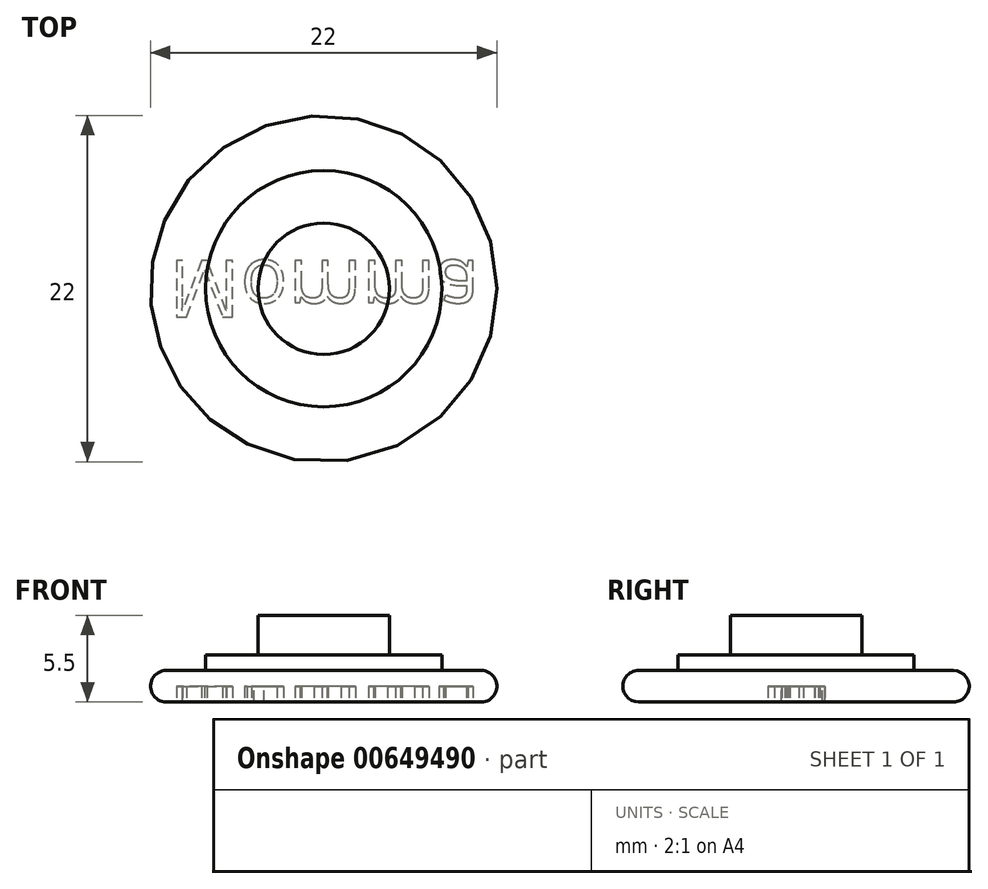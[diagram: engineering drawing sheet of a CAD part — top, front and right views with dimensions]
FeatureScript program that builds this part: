
annotation { "Feature Type Name" : "Feature", "Feature Type Description" : "" }
export const myFeature = defineFeature(function(context is Context, id is Id, definition is map)
    precondition{}
    {
        {
            var Q0;
            Q0=qCreatedBy(makeId("Top.planeOp"),FACE);
            var sketch = newSketch(context, id + "F0", { "sketchPlane" : qUnion([Q0])});
            skCircle(sketch, "E0", {"center": v(0, 0) * mm, "radius": 11 * mm});
            skCircle(sketch, "E1", {"center": v(0, 0) * mm, "radius": 7.5 * mm});
            skCircle(sketch, "E2", {"center": v(0, 0) * mm, "radius": 4.17 * mm});
            skSolve(sketch);
        }
        {
            var Q0;
            Q0=makeQuery(id+"F0.imprint","IMPRINT",FACE,{"disambiguationData":[TD([[makeQuery(id+"F0.imprint","IMPRINT",EDGE,{"derivedFrom":sQuery(id+"F0.wireOp",EDGE,"E0")}),1.0]])]});
            extrude(context, id + "F1", {"entities" : qUnion([Q0]), "depth" : 2 * mm, "offsetDistance" : 25 * mm});
        }
        {
            var Q0;
            Q0=makeQuery(id+"F0.imprint","IMPRINT",FACE,{"disambiguationData":[TD([[makeQuery(id+"F0.imprint","IMPRINT",EDGE,{"derivedFrom":sQuery(id+"F0.wireOp",EDGE,"E1")}),1.0]])]});
            extrude(context, id + "F2", {"entities" : qUnion([Q0]), "operationType" : NewBodyOperationType.ADD, "depth" : 3 * mm, "offsetDistance" : 25 * mm});
        }
        {
            var Q0;
            Q0=makeQuery(id+"F0.imprint","IMPRINT",FACE,{"disambiguationData":[TD([[makeQuery(id+"F0.imprint","IMPRINT",EDGE,{"derivedFrom":sQuery(id+"F0.wireOp",EDGE,"E2")}),1.0]])]});
            extrude(context, id + "F3", {"entities" : qUnion([Q0]), "operationType" : NewBodyOperationType.ADD, "depth" : 5.5 * mm, "offsetDistance" : 25 * mm});
        }
        {
            var Q0;
            Q0=makeQuery(id+"F1.opExtrude","CAP_EDGE",EDGE,{"disambiguationData":[OSD([sQuery(id+"F0.wireOp",EDGE,"E0")])],"isStart":false});
            var Q1;
            Q1=makeQuery(id+"F1.opExtrude","CAP_EDGE",EDGE,{"disambiguationData":[OSD([sQuery(id+"F0.wireOp",EDGE,"E0")])],"isStart":true});
            fillet(context, id + "F4", {"entities" : qUnion([Q0, Q1]), "radius" : 1 * mm, "tangentPropagation" : true, "allowEdgeOverflow" : false});
        }
        {
            var Q0;
            {var subQ0=sQuery(id+"F0.wireOp",EDGE,"E2");var subQ1=sQuery(id+"F0.wireOp",EDGE,"E1");Q0=makeQuery(id+"F3.boolean.opBoolean","MERGE",FACE,{"derivedFrom":[makeQuery(id+"F2.boolean.opBoolean","MERGE",FACE,{"derivedFrom":[makeQuery(id+"F1.opExtrude","CAP_FACE",FACE,{"disambiguationData":[OSD([sQuery(id+"F0.wireOp",EDGE,"E0"),subQ1])],"isStart":true}),makeQuery(id+"F2.opExtrude","CAP_FACE",FACE,{"disambiguationData":[OSD([subQ1,subQ0])],"isStart":true})]}),makeQuery(id+"F3.opExtrude","CAP_FACE",FACE,{"disambiguationData":[OSD([subQ0])],"isStart":true})]});}
            var sketch = newSketch(context, id + "F5", { "sketchPlane" : qUnion([Q0])});
            skText(sketch, "E3", { "text": "Momma", "fontName": "OpenSans-Regular.ttf"});
            const initialGuessF5  = {"E3": [-0.00984, -0.0018, 1, 0, 0.00362]};
            skSetInitialGuess(sketch, initialGuessF5);
            skSolve(sketch);
        }
        {
            var Q0;
            Q0 = qSketchRegion(id + "F5", true);
            extrude(context, id + "F6", {"entities" : qUnion([Q0]), "operationType" : NewBodyOperationType.REMOVE, "oppositeDirection" : true, "depth" : 1 * mm, "offsetDistance" : 25 * mm});
        }
    });
